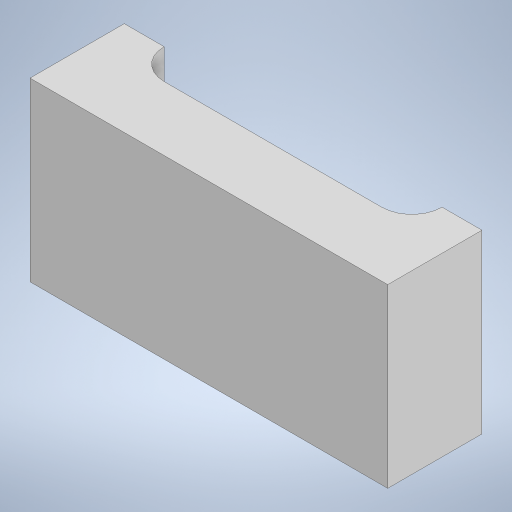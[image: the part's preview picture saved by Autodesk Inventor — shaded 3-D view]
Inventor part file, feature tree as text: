
AUTODESK INVENTOR PART (.ipt)
format: ipt  version: 2023 (Build 270158000, 158)  size: 190,976 bytes
history: native  units: mm
features: sketch x3, extrude x2, other x1, hole x1, projected_geometry x1
ambient origin geometry x8: Origin, YZ Plane, XZ Plane, XY Plane, X Axis, Y Axis, Z Axis, Center Point
bodies: Body1 (feature_tree)
feature tree (8):
  other  "Těleso1"
  extrude  "Vysunutí1"  Depth=29.6mm
  hole  "Díra1"  [1 undecoded]
  extrude  "Vysunutí2"  Depth=7.8mm TaperAngle=0.0deg
  sketch  "Náčrt1"
  sketch  "Náčrt2"
  projected_geometry  "Promítnutá smyčka1"
  sketch  "Náčrt3"
note: 1 required parameter value undecoded (feature->parameter linkage not recoverable at this tier; creation-order binding heuristic only, values carry confidence <= 0.55)
